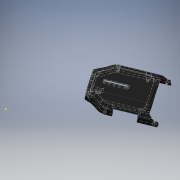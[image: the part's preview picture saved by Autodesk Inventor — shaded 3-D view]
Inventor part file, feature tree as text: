
AUTODESK INVENTOR PART (.ipt)
format: ipt  version: 2016 (Build 200138000, 138)  size: 4,610,048 bytes
history: native  units: in
note: dims shown in document units (in); Inventor stores cm internally (conversion verified against a paired STEP export)
features: extrude x58, sketch x55, projected_geometry x47, fillet x37, other x15, chamfer x14, plane x10, hole x3, mirror x3, sweep x2, shell x1, split x1
ambient origin geometry x8: Origin, YZ Plane, XZ Plane, XY Plane, X Axis, Y Axis, Z Axis, Center Point
bodies: Body1 (feature_tree), Body2 (feature_tree), Body3 (feature_tree), Body4 (feature_tree), Body5 (feature_tree), Body6 (feature_tree), Body7 (feature_tree), Body8 (feature_tree), Body9 (feature_tree), Body10 (feature_tree)
feature tree (246):
  other  "deck_ehlerscutter.ipt"
  plane  "Work Plane1"
  extrude  "Extrusion1"  Depth=0.3937in
  fillet  "Fillet1"  Radius=0.481in
  extrude  "Extrusion2"  Depth=13.7795in
  extrude  "Extrusion3"  Depth=0.7874in
  chamfer  "Chamfer2"  Distance=0.125in
  extrude  "Extrusion5"  Depth=5.5118in
  chamfer  "Chamfer5"  Distance=0.125in Angle=45.0deg
  fillet  "Fillet8"  Radius=0.315in
  fillet  "Fillet9"  Radius=11.0in
  fillet  "Fillet10"  Radius=1.1811in
  fillet  "Fillet11"  Radius=0.7874in
  chamfer  "Chamfer6"  Distance=0.3937in Angle=45.0deg
  fillet  "Fillet12"  Radius=1.9685in
  chamfer  "Chamfer7"  Distance=0.3937in Angle=45.0deg
  fillet  "Fillet13"  Radius=1.5748in
  plane  "Work Plane2"
  shell  "Shell1"  Thickness=0.2756in
  extrude  "Extrusion9"  Depth=5.6299in
  sketch  "Sketch8"  dims[d13=0.7874in]
  extrude  "Extrusion8"  Depth=0.2756in
  extrude  "Extrusion10"  Depth=1.378in
  sketch  "Sketch12"  dims[d40=0.3937in d41=0.125in d42=45.0deg d43=1.1811in d44=0.7874in]
  plane  "Work Plane3"
  extrude  "Extrusion61"  Depth=11.0in
  extrude  "Extrusion62"  Depth=1.0in
  plane  "Work Plane4"
  extrude  "Extrusion12"  Depth=0.5512in
  fillet  "Fillet14"  Radius=0.5118in
  chamfer  "Chamfer8"  Distance=1.1811in
  plane  "Work Plane5"
  extrude  "Extrusion13"  Depth=0.25in TaperAngle=45.0deg
  plane  "Work Plane6"
  extrude  "Extrusion14"  Depth=0.0787in
  other  "part_placement_sketch"
  extrude  "Extrusion16"  [1 undecoded]
  extrude  "Extrusion18"  Depth=2.126in
  extrude  "Extrusion19"  Depth=2.2441in
  extrude  "Extrusion20"  Depth=1.1811in TaperAngle=0.0deg
  chamfer  "Chamfer9"  Distance=0.8071in
  fillet  "Fillet16"  Radius=0.4724in
  fillet  "Fillet20"  Radius=0.4724in
  extrude  "Extrusion22"  Depth=0.3543in
  fillet  "Fillet30"  Radius=1.75in
  hole  "Hole1"  [1 undecoded]
  extrude  "Extrusion17"  Depth=0.1378in
  extrude  "Extrusion25"  Depth=0.1476in
  plane  "Work Plane10"
  extrude  "Extrusion28"  Depth=0.1476in
  extrude  "Extrusion42"  Depth=0.502in
  hole  "Hole2"  [1 undecoded]
  hole  "Hole3"  [1 undecoded]
  extrude  "Extrusion30"  Depth=0.315in
  extrude  "Extrusion32"  Depth=0.502in TaperAngle=0.0deg
  extrude  "Extrusion33"  Depth=1.75in
  extrude  "Extrusion34"  Depth=1.75in
  extrude  "Extrusion35"  Depth=0.0394in
  extrude  "Extrusion37"  Depth=0.0394in
  extrude  "Extrusion38"  Depth=0.375in TaperAngle=0.0deg
  extrude  "Extrusion40"  Depth=0.25in
  extrude  "Extrusion43"  Depth=0.1299in
  extrude  "Extrusion44"  Depth=0.1181in
  fillet  "Fillet24"  Radius=0.1181in
  fillet  "Fillet25"  Radius=0.1181in
  fillet  "Fillet26"  Radius=0.3543in
  fillet  "Fillet27"  Radius=0.0295in
  fillet  "Fillet28"  Radius=0.5906in
  fillet  "Fillet29"  Radius=0.3937in
  fillet  "Fillet23"  Radius=0.3543in
  extrude  "Extrusion41"  Depth=0.1772in TaperAngle=0.0deg
  extrude  "Extrusion45"  Depth=0.38in
  extrude  "Extrusion46"  Depth=0.3937in
  chamfer  "Chamfer10"  Distance=0.3937in
  plane  "Work Plane11"
  sketch  "Sketch46"  dims[d120=2.2047in]
  extrude  "Extrusion48"  Depth=0.25in TaperAngle=45.0deg
  extrude  "Extrusion49"  Depth=0.25in
  extrude  "Extrusion50"  Depth=0.25in
  extrude  "Extrusion52"  Depth=0.25in
  extrude  "Extrusion53"  Depth=0.25in TaperAngle=0.0deg
  fillet  "Fillet31"  Radius=0.201in
  extrude  "Extrusion54"  Depth=0.25in TaperAngle=0.0deg
  extrude  "Extrusion55"  Depth=0.25in
  fillet  "Fillet32"  Radius=0.3937in
  fillet  "Fillet33"  Radius=0.1575in
  extrude  "Extrusion56"  Depth=0.25in
  extrude  "Extrusion57"  Depth=0.25in TaperAngle=0.0deg
  extrude  "Extrusion58"  Depth=0.25in
  fillet  "Fillet36"  Radius=0.0591in
  extrude  "Extrusion60"  Depth=0.25in
  fillet  "Fillet42"  Radius=1.752in
  fillet  "Fillet43"  Radius=0.2362in
  fillet  "Fillet44"  Radius=0.2244in
  fillet  "Fillet45"  Radius=0.2244in
  fillet  "Fillet46"  Radius=0.2244in
  extrude  "Extrusion63"  Depth=0.25in TaperAngle=0.0deg
  fillet  "Fillet47"  Radius=0.315in
  fillet  "Fillet48"  Radius=0.9843in
  fillet  "Fillet49"  Radius=1.0in
  extrude  "Extrusion64"  Depth=0.25in
  mirror  "Mirror1"
  extrude  "Extrusion65"  Depth=0.25in
  mirror  "Mirror2"
  sketch  "Sketch63"  dims[d150=0.5512in d151=0.502in d152=0.0in]
  extrude  "Extrusion66"  Depth=0.25in TaperAngle=0.0deg
  extrude  "Extrusion67"  Depth=0.25in
  chamfer  "Chamfer11"  Distance=2.2244in
  chamfer  "Chamfer12"  Distance=0.3937in
  chamfer  "Chamfer13"  Distance=0.3937in
  sketch  "Sketch66"  dims[d158=0.1181in d159=0.0394in]
  plane  "Work Plane12"
  sketch  "Sketch67"  dims[d160=0.0625in d161=0.0394in]
  split  "Split1"
  sweep  "Sweep1"
  plane  "Work Plane13"
  extrude  "Extrusion69"  Depth=0.3937in TaperAngle=0.0deg
  chamfer  "Chamfer16"  Distance=0.1181in
  fillet  "Fillet50"  Radius=0.4079in
  fillet  "Fillet51"  Radius=0.9449in
  chamfer  "Chamfer17"  Distance=0.1181in
  fillet  "Fillet55"  Radius=0.2362in
  extrude  "Extrusion74"  TaperAngle=0.0deg  [1 undecoded]
  extrude  "Extrusion75"  Depth=0.3937in
  fillet  "Fillet56"  Radius=0.1181in
  fillet  "Fillet57"  Radius=0.1969in
  chamfer  "Chamfer18"  Distance=0.1181in
  extrude  "Extrusion70"  Depth=0.25in
  extrude  "Extrusion71"  Depth=0.25in
  extrude  "Extrusion72"  Depth=0.25in
  mirror  "Mirror3"
  extrude  "Extrusion73"  Depth=0.25in TaperAngle=0.0deg
  chamfer  "Chamfer19"  Distance=0.0295in
  fillet  "Fillet58"  Radius=0.0197in
  fillet  "Fillet59"  [1 undecoded]
  extrude  "Extrusion76"  TaperAngle=45.0deg  [1 undecoded]
  sketch  "Sketch78"  dims[d231=0.21in d232=0.75in d233=0.375in d234=0.25in d235=0.5635in d236=1.0in d237=0.8108in d238=0.159in d239=0.75in d240=0.375in d241=0.25in d242=0.5635in d243=1.0in d244=0.8108in d245=0.1575in d246=0.125in d247=45.0deg d248=1.0in d249=0.38in d250=2.625in d251=0.9843in d252=0.0in d257=0.201in d258=0.9843in d259=0.0in d260=0.4724in d261=0.3937in d262=0.1575in d263=0.315in d264=2.0in d265=0.0in d267=0.2953in d268=0.0591in d269=0.0in d270=0.9646in d271=1.752in d274=0.2362in d275=0.0in d280=0.2244in d281=0.2244in d282=0.2244in d283=0.0945in d284=0.0in d285=0.315in d286=0.9843in d287=1.0in d288=0.0in d291=1.375in d292=0.3065in d296=1.063in d297=0.0in d298=0.7874in d299=2.2244in d300=0.3937in d301=0.3937in d302=0.9449in d303=0.0in d304=0.3937in d305=0.0in d306=0.1181in d307=0.4079in d308=0.9449in d309=0.0in d310=0.1181in d311=0.2362in d312=0.0in d313=0.0in d314=0.3937in d315=0.1181in d316=0.1969in d317=0.1181in d318=0.1969in d319=0.1969in d320=0.0394in d324=0.9449in d325=0.0in d329=0.0295in d330=0.0in d334=0.0197in d335=0.125in d336=45.0deg d337=45.0deg d338=45.0deg d339=1.0in d340=0.0in d341=1.0in d342=0.0in d343=0.2362in d344=0.8071in d345=1.0in d346=0.0in d351=0.2362in d352=0.3937in d353=1.0in d354=0.0in d355=0.2165in d356=0.1181in d357=1.0in d358=0.0in d359=0.1181in d360=0.1969in d361=0.2362in d362=0.0in d363=0.1772in d364=0.1181in d365=0.0in d366=0.0787in d367=0.0787in d369=0.0787in d370=0.0in d371=2.2in d372=3.05in d373=0.0787in d374=0.0in d376=2.2in d377=3.05in d378=0.125in d379=0.0in d381=0.0625in d415=1.5748in d416=1.5748in d417=0.0984in d418=0.6299in d419=0.6299in d420=1.5748in d422=360.0deg d424=0.0787in d425=1.5748in d427=0.1575in d428=1.5748in d430=0.1575in d433=0.125in d434=0.0in d435=1.1811in d436=0.0394in d437=0.125in d438=0.8986in d439=0.0in d440=0.0in d441=0.125in d442=0.0in d443=4.0in d444=10.0in d445=0.125in d446=1.0in d447=0.0in d448=0.0394in d449=0.0625in d450=0.25in d451=0.201in d452=0.375in d453=0.75in d454=3.937in d456=0.875in d457=0.3937in d459=1.0in d461=1.0in d462=0.0in d463=0.1616in d464=3.937in d466=0.875in d467=0.3937in d469=1.0in d471=0.0625in d472=0.0in d473=0.7677in d474=0.8071in d475=0.0787in d476=0.0in d477=0.0394in d479=0.2362in d480=0.4331in d481=0.2165in d482=0.0787in d483=0.0in d484=0.0197in d485=0.125in d486=45.0deg d487=0.0787in d488=0.125in d489=45.0deg d490=0.0625in d491=0.125in d492=45.0deg d493=75.0deg d495=1.0994in d496=90.0deg d497=18.0in d498=0.0in d499=0.0in d506=0.0in d507=0.0in d515=2.3622in d516=0.0787in d519=4.0in d520=4.0in d521=0.7874in d522=0.0in d523=0.0787in d524=0.125in d525=45.0deg d526=0.2362in d527=0.0787in d528=0.2362in d529=0.125in d530=45.0deg d531=0.0787in d532=0.125in d533=45.0deg d536=1.5in d537=1.5in d538=0.7874in d539=0.0in d540=0.125in d541=0.25in d542=0.375in d543=0.7874in d544=0.0in d546=0.5in d547=0.125in d548=0.0in d549=0.5in d551=0.21in d552=0.0625in d553=0.0in d554=0.125in d557=0.125in d558=0.25in d559=0.0394in d560=0.0591in d561=0.0in d562=0.0in d563=0.0197in d564=0.0in d565=0.375in d566=0.25in d567=0.0984in d568=0.125in d569=45.0deg d570=0.2756in d571=0.25in d574=0.25in d575=0.0197in d576=0.5in d577=0.125in d578=0.0in d579=1.2093in d580=1.2093in]
  other  "Solid1::deck_ehlerscutter.ipt"
  other  "TaggingFeature1"
  sketch  "Sketch1"  dims[d0=0.3937in d1=0.7874in d2=0.481in]
  projected_geometry  "Projected Loop1"
  other  "sink"
  sketch  "Sketch2"  dims[d3=0.481in d4=13.7795in]
  projected_geometry  "Projected Loop2"
  other  "curve"
  sketch  "Sketch3"  dims[d5=0.125in d6=0.0in d7=0.7874in d9=0.125in d10=0.0in]
  projected_geometry  "Projected Loop3"
  other  "print"
  sketch  "Sketch5"  dims[d11=4.0in d12=5.5118in]
  sketch  "Sketch9"  dims[d15=0.0in]
  sketch  "Sketch10"  dims[d22=1.378in d23=0.125in d24=45.0deg d25=0.315in d26=11.0in d27=0.0in]
  projected_geometry  "Projected Loop6"
  sketch  "Sketch13"  dims[d45=11.811in]
  sketch  "Sketch14"  dims[d46=1.1811in d47=0.3937in d48=0.125in d49=45.0deg d50=1.9685in d51=0.3937in d52=0.125in d53=45.0deg d54=1.5748in d60=0.2756in]
  sketch  "Sketch17"  dims[d65=3.9764in d66=5.6299in]
  other  "esc_clamp"
  sketch  "Sketch18"  dims[d67=0.8986in d68=0.0in d69=0.2756in]
  projected_geometry  "Projected Loop9"
  projected_geometry  "Projected Loop10"
  sketch  "Sketch19"  dims[d70=1.8898in d71=1.378in]
  projected_geometry  "Projected Loop11"
  sketch  "Sketch21"  dims[d72=0.8986in d73=0.0in d74=11.0in]
  projected_geometry  "Projected Loop12"
  projected_geometry  "Projected Loop13"
  projected_geometry  "Projected Loop14"
  sketch  "Sketch22"  dims[d75=0.8986in d76=0.0in d88=1.0in]
  sketch  "Sketch25"  dims[d89=0.5512in d90=0.5512in d91=0.5118in]
  projected_geometry  "Projected Loop17"
  sketch  "Sketch29"  dims[d92=-1.0236in]
  sketch  "Sketch31"  dims[d93=-1.0236in d94=1.1811in d95=0.0in]
  sketch  "Sketch32"  dims[d96=0.25in d99=0.5in d100=0.125in d101=45.0deg]
  sketch  "Sketch33"  dims[d102=-0.0787in d103=0.0787in]
  projected_geometry  "Projected Loop19"
  projected_geometry  "Projected Loop20"
  sketch  "Sketch36"  dims[d104=1.1811in d105=0.0in d106=-0.0787in]
  sketch  "Sketch37"  dims[d107=0.1969in d108=2.126in]
  projected_geometry  "Projected Loop22"
  sketch  "Sketch39"  dims[d109=0.4134in d110=2.2441in]
  sketch  "Sketch40"  dims[d111=0.0591in d112=1.1811in d113=0.0in]
  projected_geometry  "Projected Loop23"
  projected_geometry  "Projected Loop24"
  projected_geometry  "Projected Loop25"
  projected_geometry  "Projected Loop26"
  projected_geometry  "Projected Loop27"
  projected_geometry  "Projected Loop28"
  sketch  "Sketch41"  dims[d116=1.3976in]
  sketch  "Sketch42"  dims[d117=2.0472in]
  projected_geometry  "Projected Loop29"
  sketch  "Sketch43"  dims[d118=1.3976in]
  other  "led_thing"
  sketch  "Sketch44"  dims[d119=2.0472in]
  projected_geometry  "Projected Loop30"
  sketch  "Sketch47"  dims[d121=2.5591in]
  sketch  "Sketch49"  dims[d123=0.2756in]
  projected_geometry  "Projected Loop31"
  sketch  "Sketch50"  dims[d124=0.0591in d125=0.8071in d126=0.0in d127=0.4724in d128=0.4724in]
  projected_geometry  "Projected Loop32"
  sketch  "Sketch51"  dims[d129=0.3543in d130=0.3543in d131=1.75in]
  sketch  "Sketch52"  dims[d132=0.1378in d133=0.4528in]
  sketch  "Sketch53"  dims[d134=0.3543in d135=0.1378in]
  sketch  "Sketch54"  dims[d136=0.1476in d137=0.1476in]
  sketch  "Sketch55"  dims[d138=0.1476in d139=0.1476in]
  other  "heatsinkriser"
  sketch  "Sketch57"  dims[d140=0.748in d141=0.502in]
  other  "battery"
  sketch  "Sketch60"  dims[d142=0.0787in d144=1.0in d145=0.0in]
  sketch  "Sketch61"  dims[d146=0.4724in d147=0.0394in]
  sketch  "Sketch62"  dims[d148=0.2362in d149=0.315in]
  projected_geometry  "Projected Loop35"
  sketch  "Sketch64"  dims[d153=0.1575in d154=0.0in d155=1.75in]
  projected_geometry  "Projected Loop36"
  sketch  "Sketch65"  dims[d156=0.1181in d157=1.75in]
  projected_geometry  "Projected Loop37"
  other  "Srf1"
  sketch  "Sketch68"  dims[d162=0.0625in d163=0.375in d164=0.0in]
  projected_geometry  "Projected Loop40"
  projected_geometry  "Projected Loop41"
  projected_geometry  "Projected Loop42"
  projected_geometry  "Projected Loop43"
  projected_geometry  "Projected Loop44"
  sketch  "Sketch71"  dims[d167=0.25in d168=0.1299in]
  projected_geometry  "Projected Loop45"
  projected_geometry  "Projected Loop46"
  projected_geometry  "Projected Loop47"
  projected_geometry  "Projected Loop48"
  sketch  "Sketch72"  dims[d169=0.1299in d170=0.1299in]
  projected_geometry  "Projected Loop49"
  projected_geometry  "Projected Loop50"
  sketch  "Sketch73"  dims[d171=0.1181in d172=0.1181in d173=0.1181in d174=0.1181in d175=0.3543in d176=0.0in]
  projected_geometry  "Projected Loop51"
  projected_geometry  "Projected Loop52"
  projected_geometry  "Projected Loop53"
  projected_geometry  "Projected Loop54"
  sketch  "Sketch74"  dims[d177=0.126in d178=0.75in d179=0.375in d180=0.25in d181=0.5635in d182=1.0in d183=0.8108in d199=0.0295in d200=0.5906in d201=0.3937in d202=0.3543in]
  sketch  "Sketch75"  dims[d203=0.4134in d204=0.1772in d205=0.0in]
  projected_geometry  "Projected Loop55"
  sketch  "Sketch76"  dims[d214=0.38in d217=0.38in]
  projected_geometry  "Projected Loop56"
  projected_geometry  "Projected Loop57"
  sketch  "Sketch77"  dims[d218=0.1875in d220=1.1811in d222=4.375in d223=0.3937in d225=1.0in d227=0.3937in d228=0.0in]
  projected_geometry  "Projected Loop58"
  projected_geometry  "Projected Loop59"
  other  "wood"
  sweep  "SweepSrf1"
  other  "print_front"
  other  "print_back"
note: 7 required parameter values undecoded (feature->parameter linkage not recoverable at this tier; creation-order binding heuristic only, values carry confidence <= 0.55)
